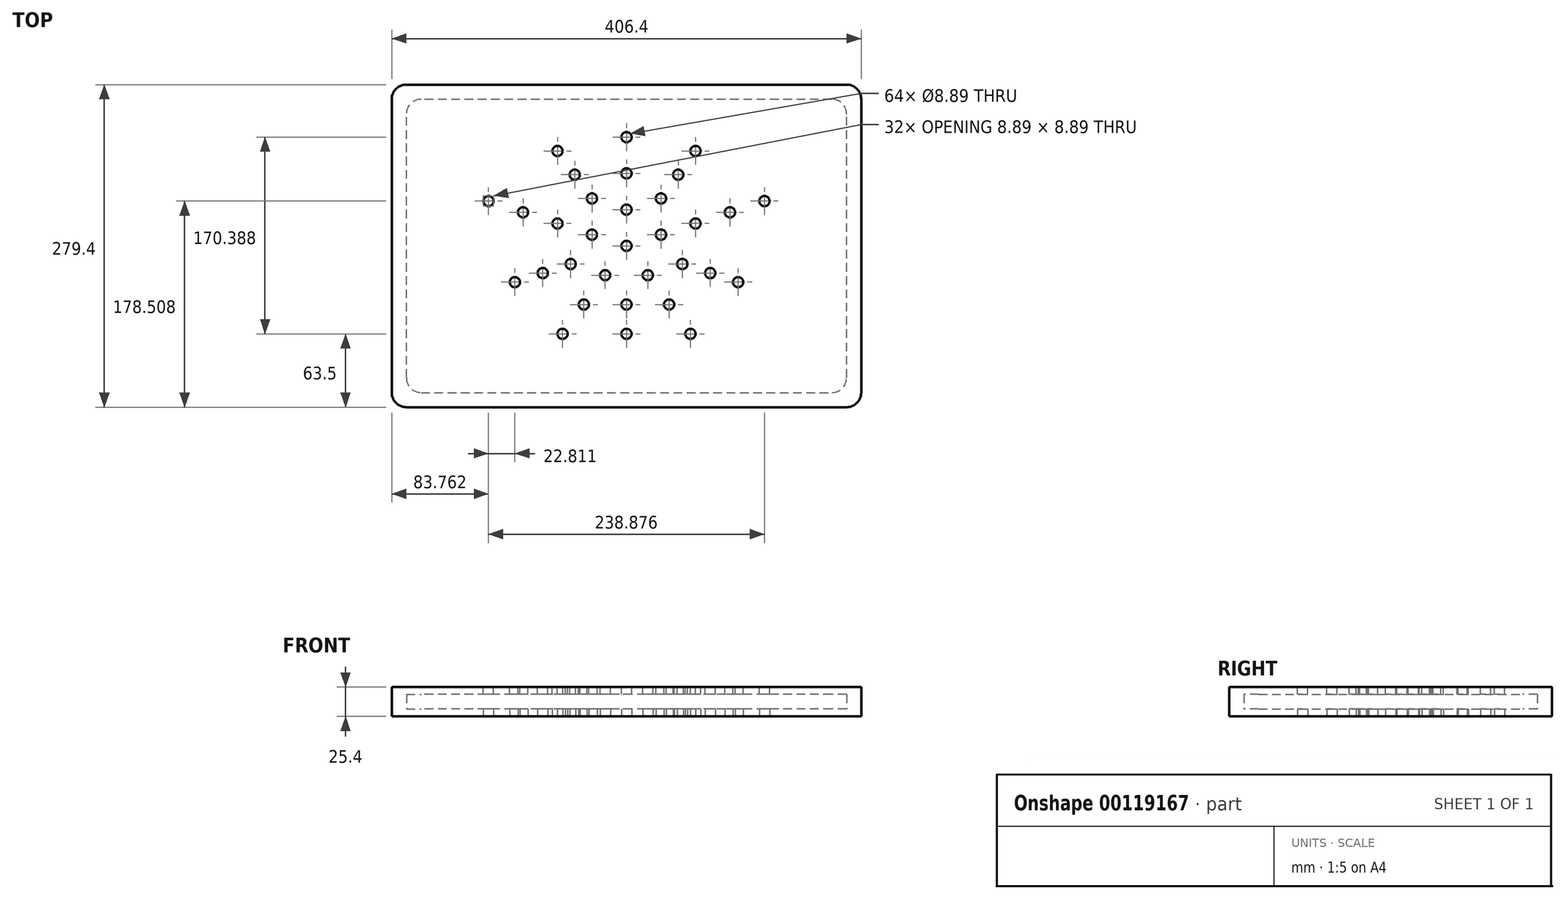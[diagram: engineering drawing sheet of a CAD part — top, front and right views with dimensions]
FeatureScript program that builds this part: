
annotation { "Feature Type Name" : "Feature", "Feature Type Description" : "" }
export const myFeature = defineFeature(function(context is Context, id is Id, definition is map)
    precondition{}
    {
        {
            var Q0;
            Q0=qCreatedBy(makeId("Top.planeOp"),FACE);
            var sketch = newSketch(context, id + "F0", { "sketchPlane" : qUnion([Q0])});
            skLineSegment(sketch, "E0", {"start": v(0, 139.7) * mm, "end": v(190.5, 139.7) * mm});
            skLineSegment(sketch, "E1", {"start": v(203.2, 127) * mm, "end": v(203.2, 0) * mm});
            skLineSegment(sketch, "E2.MirrorCS", {"start": v(0, 139.7) * mm, "end": v(-190.5, 139.7) * mm});
            skLineSegment(sketch, "E3.MirrorCS", {"start": v(-203.2, 127) * mm, "end": v(-203.2, 0) * mm});
            skLineSegment(sketch, "E4.MirrorCS", {"start": v(-203.2, -127) * mm, "end": v(-203.2, 0) * mm});
            skLineSegment(sketch, "E5.MirrorCS", {"start": v(0, -139.7) * mm, "end": v(-190.5, -139.7) * mm});
            skLineSegment(sketch, "E6.MirrorCS", {"start": v(0, -139.7) * mm, "end": v(190.5, -139.7) * mm});
            skLineSegment(sketch, "E7.MirrorCS", {"start": v(203.2, -127) * mm, "end": v(203.2, 0) * mm});
            skPoint(sketch, "E8.visualSharp", {"position": v(-203.2, 139.7) * mm});
            skArc(sketch, "E8.filletArc", {"start": v(-190.5, 139.7) * mm, "mid": v(-199.48, 135.98) * mm, "end": v(-203.2, 127) * mm});
            skPoint(sketch, "E9.visualSharp", {"position": v(203.2, 139.7) * mm});
            skArc(sketch, "E9.filletArc", {"start": v(203.2, 127) * mm, "mid": v(199.48, 135.98) * mm, "end": v(190.5, 139.7) * mm});
            skPoint(sketch, "E10.visualSharp", {"position": v(203.2, -139.7) * mm});
            skArc(sketch, "E10.filletArc", {"start": v(190.5, -139.7) * mm, "mid": v(199.48, -135.98) * mm, "end": v(203.2, -127) * mm});
            skPoint(sketch, "E11.visualSharp", {"position": v(-203.2, -139.7) * mm});
            skArc(sketch, "E11.filletArc", {"start": v(-203.2, -127) * mm, "mid": v(-199.48, -135.98) * mm, "end": v(-190.5, -139.7) * mm});
            skLineSegment(sketch, "E12", {"start": v(190.5, 114.3) * mm, "end": v(190.5, -114.3) * mm});
            skLineSegment(sketch, "E13", {"start": v(177.8, -127) * mm, "end": v(-177.8, -127) * mm});
            skLineSegment(sketch, "E14", {"start": v(-190.5, 114.3) * mm, "end": v(-190.5, -114.3) * mm});
            skLineSegment(sketch, "E15", {"start": v(-177.8, 127) * mm, "end": v(177.8, 127) * mm});
            skArc(sketch, "E16.filletArc", {"start": v(-177.8, 127) * mm, "mid": v(-186.78, 123.28) * mm, "end": v(-190.5, 114.3) * mm});
            skArc(sketch, "E17.filletArc", {"start": v(-190.5, -114.3) * mm, "mid": v(-186.78, -123.28) * mm, "end": v(-177.8, -127) * mm});
            skArc(sketch, "E18.filletArc", {"start": v(177.8, -127) * mm, "mid": v(186.78, -123.28) * mm, "end": v(190.5, -114.3) * mm});
            skArc(sketch, "E19.filletArc", {"start": v(190.5, 114.3) * mm, "mid": v(186.78, 123.28) * mm, "end": v(177.8, 127) * mm});
            skSolve(sketch);
        }
        {
            var Q0;
            Q0 = qSketchRegion(id + "F0", true);
            var Q1;
            Q1=makeQuery(id+"F0.imprint","IMPRINT",FACE,{"disambiguationData":[TD([[makeQuery(id+"F0.imprint","IMPRINT",EDGE,{"derivedFrom":sQuery(id+"F0.wireOp",EDGE,"E12")}),-1.0]])]});
            extrude(context, id + "F1", {"entities" : qUnion([Q0, Q1]), "depth" : 6.35 * mm});
        }
        {
            var Q0;
            Q0=makeQuery(id+"F0.imprint","IMPRINT",FACE,{"disambiguationData":[TD([[makeQuery(id+"F0.imprint","IMPRINT",EDGE,{"derivedFrom":sQuery(id+"F0.wireOp",EDGE,"E0")}),-1.0]])]});
            extrude(context, id + "F2", {"entities" : qUnion([Q0]), "operationType" : NewBodyOperationType.ADD, "depth" : 12.7 * mm});
        }
        {
            var Q0;
            Q0=makeQuery(id+"F0.imprint","IMPRINT",FACE,{"disambiguationData":[TD([[makeQuery(id+"F0.imprint","IMPRINT",EDGE,{"derivedFrom":sQuery(id+"F0.wireOp",EDGE,"E12")}),-1.0]])]});
            var sketch = newSketch(context, id + "F3", { "sketchPlane" : qUnion([Q0])});
            skCircle(sketch, "E20.cCircle", {"center": v(0, 0) * mm, "radius": 25.4 * mm, "construction": true});
            skLineSegment(sketch, "E20.0", {"start": v(18.45, -25.4) * mm, "end": v(-18.45, -25.4) * mm});
            skLineSegment(sketch, "E20.1", {"start": v(-18.45, -25.4) * mm, "end": v(-29.86, 9.7) * mm});
            skLineSegment(sketch, "E20.2", {"start": v(-29.86, 9.7) * mm, "end": v(0, 31.4) * mm});
            skLineSegment(sketch, "E20.3", {"start": v(0, 31.4) * mm, "end": v(29.86, 9.7) * mm});
            skLineSegment(sketch, "E20.4", {"start": v(29.86, 9.7) * mm, "end": v(18.45, -25.4) * mm});
            skPoint(sketch, "E21", {"position": v(-18.45, -25.4) * mm});
            skPoint(sketch, "E22", {"position": v(-29.86, 9.7) * mm});
            skPoint(sketch, "E23", {"position": v(0, 31.4) * mm});
            skPoint(sketch, "E24", {"position": v(29.86, 9.7) * mm});
            skPoint(sketch, "E25", {"position": v(18.45, -25.4) * mm});
            skCircle(sketch, "E26.cCircle", {"center": v(0, 0) * mm, "radius": 50.8 * mm, "construction": true});
            skLineSegment(sketch, "E26.0", {"start": v(36.9, -50.8) * mm, "end": v(-36.9, -50.8) * mm});
            skLineSegment(sketch, "E26.1", {"start": v(-36.9, -50.8) * mm, "end": v(-59.72, 19.4) * mm});
            skLineSegment(sketch, "E26.2", {"start": v(-59.72, 19.4) * mm, "end": v(0, 62.8) * mm});
            skLineSegment(sketch, "E26.3", {"start": v(0, 62.8) * mm, "end": v(59.72, 19.4) * mm});
            skLineSegment(sketch, "E26.4", {"start": v(59.72, 19.4) * mm, "end": v(36.9, -50.8) * mm});
            skPoint(sketch, "E26.0.midPoint", {"position": v(0, -50.8) * mm});
            skCircle(sketch, "E27.cCircle", {"center": v(0, 0) * mm, "radius": 76.2 * mm, "construction": true});
            skLineSegment(sketch, "E27.0", {"start": v(55.36, -76.2) * mm, "end": v(-55.36, -76.2) * mm});
            skLineSegment(sketch, "E27.1", {"start": v(-55.36, -76.2) * mm, "end": v(-89.58, 29.1) * mm});
            skLineSegment(sketch, "E27.2", {"start": v(-89.58, 29.1) * mm, "end": v(0, 94.19) * mm});
            skLineSegment(sketch, "E27.3", {"start": v(0, 94.19) * mm, "end": v(89.58, 29.1) * mm});
            skLineSegment(sketch, "E27.4", {"start": v(89.58, 29.1) * mm, "end": v(55.36, -76.2) * mm});
            skPoint(sketch, "E27.0.midPoint", {"position": v(0, -76.2) * mm});
            skPoint(sketch, "E28", {"position": v(-55.36, -76.2) * mm});
            skPoint(sketch, "E29", {"position": v(-36.9, -50.8) * mm});
            skPoint(sketch, "E30", {"position": v(36.9, -50.8) * mm});
            skPoint(sketch, "E31", {"position": v(55.36, -76.2) * mm});
            skPoint(sketch, "E32", {"position": v(59.72, 19.4) * mm});
            skPoint(sketch, "E33", {"position": v(0, 62.8) * mm});
            skPoint(sketch, "E34", {"position": v(-59.72, 19.4) * mm});
            skPoint(sketch, "E35", {"position": v(-89.58, 29.1) * mm});
            skPoint(sketch, "E36", {"position": v(-72.47, -23.55) * mm});
            skPoint(sketch, "E37", {"position": v(72.47, -23.55) * mm});
            skPoint(sketch, "E38", {"position": v(0, 94.19) * mm});
            skPoint(sketch, "E39", {"position": v(-44.79, 61.65) * mm});
            skPoint(sketch, "E40", {"position": v(44.79, 61.65) * mm});
            skPoint(sketch, "E41", {"position": v(29.86, 41.1) * mm});
            skPoint(sketch, "E42", {"position": v(48.31, -15.7) * mm});
            skPoint(sketch, "E43", {"position": v(-48.31, -15.7) * mm});
            skPoint(sketch, "E44", {"position": v(-29.86, 41.1) * mm});
            skCircle(sketch, "E45.cCircle", {"center": v(0, 0) * mm, "radius": 101.6 * mm, "construction": true});
            skLineSegment(sketch, "E45.0", {"start": v(73.82, -101.6) * mm, "end": v(-73.82, -101.6) * mm});
            skLineSegment(sketch, "E45.1", {"start": v(-73.82, -101.6) * mm, "end": v(-119.44, 38.8) * mm});
            skLineSegment(sketch, "E45.2", {"start": v(-119.44, 38.8) * mm, "end": v(0, 125.58) * mm});
            skLineSegment(sketch, "E45.3", {"start": v(0, 125.58) * mm, "end": v(119.44, 38.8) * mm});
            skLineSegment(sketch, "E45.4", {"start": v(119.44, 38.8) * mm, "end": v(73.82, -101.6) * mm});
            skPoint(sketch, "E45.0.midPoint", {"position": v(0, -101.6) * mm});
            skPoint(sketch, "E46", {"position": v(-96.63, -31.4) * mm});
            skPoint(sketch, "E47", {"position": v(-119.44, 38.8) * mm});
            skPoint(sketch, "E48", {"position": v(-59.72, 82.2) * mm});
            skPoint(sketch, "E49", {"position": v(59.72, 82.2) * mm});
            skPoint(sketch, "E50", {"position": v(119.44, 38.8) * mm});
            skPoint(sketch, "E51", {"position": v(96.63, -31.4) * mm});
            skSolve(sketch);
        }
        {
            var Q0;
            Q0=sQuery(id+"F3.wireOp",VERTEX,"E25");
            var Q1;
            Q1=sQuery(id+"F3.wireOp",VERTEX,"E21");
            var Q2;
            Q2=sQuery(id+"F3.wireOp",VERTEX,"E22");
            var Q3;
            Q3=sQuery(id+"F3.wireOp",VERTEX,"E23");
            var Q4;
            Q4=sQuery(id+"F3.wireOp",VERTEX,"E24");
            var Q5;
            Q5=sQuery(id+"F3.wireOp",VERTEX,"9678e8b7-a6e0-4f8e-94d9-639228b9ece8");
            var Q6;
            Q6=sQuery(id+"F3.wireOp",VERTEX,"abd06c31-787e-49ee-9a94-d06c42999d1f");
            var Q7;
            Q7=sQuery(id+"F3.wireOp",VERTEX,"0b1b4699-1091-4c9d-986a-ef9341f31634");
            var Q8;
            Q8=sQuery(id+"F3.wireOp",VERTEX,"2714ad65-7b77-42a2-b454-52a659858b10");
            var Q9;
            Q9=sQuery(id+"F3.wireOp",VERTEX,"4cc9f397-6185-4efe-b508-18939f6c2ec1");
            var Q10;
            Q10=sQuery(id+"F3.wireOp",VERTEX,"ff00e035-120a-44ff-9a1f-e55fb384b807");
            var Q11;
            Q11=sQuery(id+"F3.wireOp",VERTEX,"E20.cCircle.center");
            var Q12;
            Q12=sQuery(id+"F3.wireOp",VERTEX,"E29");
            var Q13;
            Q13=sQuery(id+"F3.wireOp",VERTEX,"E26.0.midPoint");
            var Q14;
            Q14=sQuery(id+"F3.wireOp",VERTEX,"E30");
            var Q15;
            Q15=sQuery(id+"F3.wireOp",VERTEX,"E32");
            var Q16;
            Q16=sQuery(id+"F3.wireOp",VERTEX,"E33");
            var Q17;
            Q17=sQuery(id+"F3.wireOp",VERTEX,"E34");
            var Q18;
            Q18=sQuery(id+"F3.wireOp",VERTEX,"E36");
            var Q19;
            Q19=sQuery(id+"F3.wireOp",VERTEX,"E28");
            var Q20;
            Q20=sQuery(id+"F3.wireOp",VERTEX,"E27.0.midPoint");
            var Q21;
            Q21=sQuery(id+"F3.wireOp",VERTEX,"E31");
            var Q22;
            Q22=sQuery(id+"F3.wireOp",VERTEX,"E37");
            var Q23;
            Q23=sQuery(id+"F3.wireOp",VERTEX,"E27.4.start");
            var Q24;
            Q24=sQuery(id+"F3.wireOp",VERTEX,"E40");
            var Q25;
            Q25=sQuery(id+"F3.wireOp",VERTEX,"E38");
            var Q26;
            Q26=sQuery(id+"F3.wireOp",VERTEX,"E39");
            var Q27;
            Q27=sQuery(id+"F3.wireOp",VERTEX,"E35");
            var Q28;
            Q28=sQuery(id+"F3.wireOp",VERTEX,"E43");
            var Q29;
            Q29=sQuery(id+"F3.wireOp",VERTEX,"E44");
            var Q30;
            Q30=sQuery(id+"F3.wireOp",VERTEX,"E41");
            var Q31;
            Q31=sQuery(id+"F3.wireOp",VERTEX,"E42");
            var Q32;
            Q32=sQuery(id+"F3.wireOp",VERTEX,"E46");
            var Q33;
            Q33=sQuery(id+"F3.wireOp",VERTEX,"E47");
            var Q34;
            Q34=sQuery(id+"F3.wireOp",VERTEX,"E48");
            var Q35;
            Q35=sQuery(id+"F3.wireOp",VERTEX,"E49");
            var Q36;
            Q36=sQuery(id+"F3.wireOp",VERTEX,"E50");
            var Q37;
            Q37=sQuery(id+"F3.wireOp",VERTEX,"E51");
            var Q38;
            Q38=makeQuery(id+"F1.opExtrude","SWEPT_BODY",BODY,{"disambiguationData":[OSD([sQuery(id+"F0.wireOp",EDGE,"E0"),sQuery(id+"F0.wireOp",EDGE,"E1"),sQuery(id+"F0.wireOp",EDGE,"E2.MirrorCS"),sQuery(id+"F0.wireOp",EDGE,"E3.MirrorCS"),sQuery(id+"F0.wireOp",EDGE,"E4.MirrorCS"),sQuery(id+"F0.wireOp",EDGE,"E5.MirrorCS"),sQuery(id+"F0.wireOp",EDGE,"E6.MirrorCS"),sQuery(id+"F0.wireOp",EDGE,"E7.MirrorCS"),sQuery(id+"F0.wireOp",EDGE,"E8.filletArc"),sQuery(id+"F0.wireOp",EDGE,"E9.filletArc"),sQuery(id+"F0.wireOp",EDGE,"E10.filletArc"),sQuery(id+"F0.wireOp",EDGE,"E11.filletArc")])]});
            hole(context, id + "F4", {"style" : HoleStyle.SIMPLE, "endStyle" : HoleEndStyle.BLIND, "oppositeDirection" : true, "holeDiameter" : 8.9 * mm, "holeDepth" : 12.7 * mm, "startFromSketch" : true, "locations" : qUnion([Q0, Q1, Q2, Q3, Q4, Q5, Q6, Q7, Q8, Q9, Q10, Q11, Q12, Q13, Q14, Q15, Q16, Q17, Q18, Q19, Q20, Q21, Q22, Q23, Q24, Q25, Q26, Q27, Q28, Q29, Q30, Q31, Q32, Q33, Q34, Q35, Q36, Q37]), "scope" : qUnion([Q38])});
        }
        {
            var Q0;
            Q0=makeQuery(id+"F1.opExtrude","SWEPT_BODY",BODY,{"disambiguationData":[OSD([sQuery(id+"F0.wireOp",EDGE,"E0"),sQuery(id+"F0.wireOp",EDGE,"E1"),sQuery(id+"F0.wireOp",EDGE,"E2.MirrorCS"),sQuery(id+"F0.wireOp",EDGE,"E3.MirrorCS"),sQuery(id+"F0.wireOp",EDGE,"E4.MirrorCS"),sQuery(id+"F0.wireOp",EDGE,"E5.MirrorCS"),sQuery(id+"F0.wireOp",EDGE,"E6.MirrorCS"),sQuery(id+"F0.wireOp",EDGE,"E7.MirrorCS"),sQuery(id+"F0.wireOp",EDGE,"E8.filletArc"),sQuery(id+"F0.wireOp",EDGE,"E9.filletArc"),sQuery(id+"F0.wireOp",EDGE,"E10.filletArc"),sQuery(id+"F0.wireOp",EDGE,"E11.filletArc")])]});
            var Q1;
            Q1=makeQuery(id+"F2.opExtrude","CAP_FACE",FACE,{"disambiguationData":[OSD([sQuery(id+"F0.wireOp",EDGE,"E0"),sQuery(id+"F0.wireOp",EDGE,"E1"),sQuery(id+"F0.wireOp",EDGE,"E2.MirrorCS"),sQuery(id+"F0.wireOp",EDGE,"E3.MirrorCS"),sQuery(id+"F0.wireOp",EDGE,"E4.MirrorCS"),sQuery(id+"F0.wireOp",EDGE,"E5.MirrorCS"),sQuery(id+"F0.wireOp",EDGE,"E6.MirrorCS"),sQuery(id+"F0.wireOp",EDGE,"E7.MirrorCS"),sQuery(id+"F0.wireOp",EDGE,"E8.filletArc"),sQuery(id+"F0.wireOp",EDGE,"E9.filletArc"),sQuery(id+"F0.wireOp",EDGE,"E10.filletArc"),sQuery(id+"F0.wireOp",EDGE,"E11.filletArc"),sQuery(id+"F0.wireOp",EDGE,"E12"),sQuery(id+"F0.wireOp",EDGE,"E13"),sQuery(id+"F0.wireOp",EDGE,"E14"),sQuery(id+"F0.wireOp",EDGE,"E15"),sQuery(id+"F0.wireOp",EDGE,"E16.filletArc"),sQuery(id+"F0.wireOp",EDGE,"E17.filletArc"),sQuery(id+"F0.wireOp",EDGE,"E18.filletArc"),sQuery(id+"F0.wireOp",EDGE,"E19.filletArc")])],"isStart":false});
            mirror(context, id + "F5", {"operationType" : NewBodyOperationType.ADD, "entities" : qUnion([Q0]), "mirrorPlane" : qUnion([Q1])});
        }
    });
